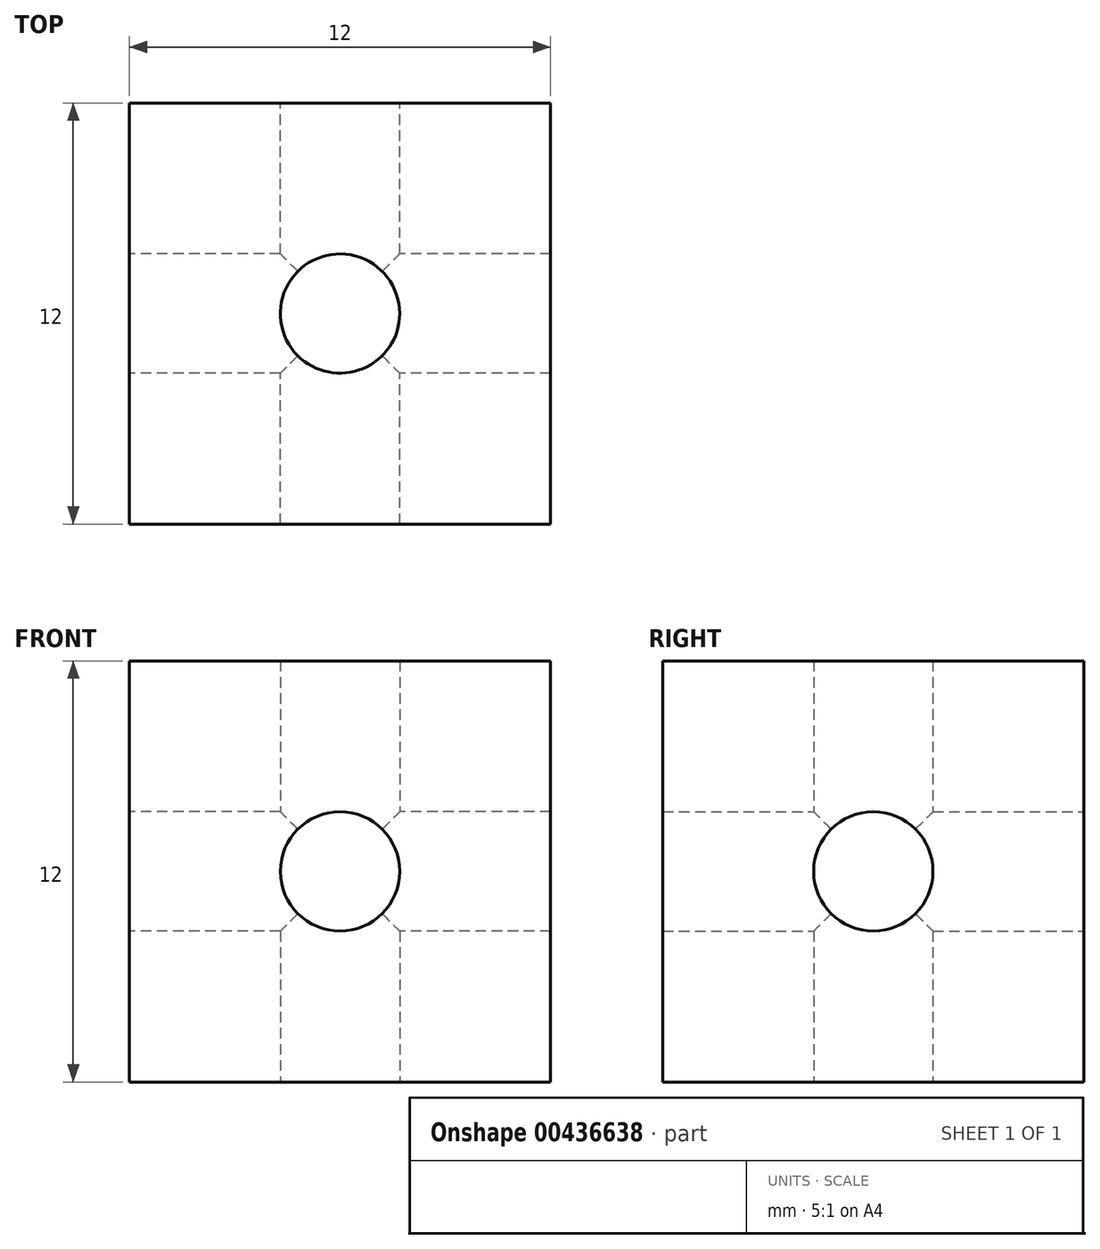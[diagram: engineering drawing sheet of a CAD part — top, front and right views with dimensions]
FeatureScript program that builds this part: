
annotation { "Feature Type Name" : "Feature", "Feature Type Description" : "" }
export const myFeature = defineFeature(function(context is Context, id is Id, definition is map)
    precondition{}
    {
        {
            var Q0;
            Q0=qCreatedBy(makeId("Top.planeOp"),FACE);
            var sketch = newSketch(context, id + "F0", { "sketchPlane" : qUnion([Q0])});
            skLineSegment(sketch, "E0.bottom", {"start": v(6, 6) * mm, "end": v(-6, 6) * mm});
            skLineSegment(sketch, "E0.top", {"start": v(6, -6) * mm, "end": v(-6, -6) * mm});
            skLineSegment(sketch, "E0.left", {"start": v(6, 6) * mm, "end": v(6, -6) * mm});
            skLineSegment(sketch, "E0.right", {"start": v(-6, 6) * mm, "end": v(-6, -6) * mm});
            skPoint(sketch, "E0.middle", {"position": v(0, 0) * mm});
            skCircle(sketch, "E1", {"center": v(0, 0) * mm, "radius": 1.7 * mm});
            skSolve(sketch);
        }
        {
            var Q0;
            Q0=makeQuery(id+"F0.imprint","IMPRINT",FACE,{"disambiguationData":[TD([[makeQuery(id+"F0.imprint","IMPRINT",EDGE,{"derivedFrom":sQuery(id+"F0.wireOp",EDGE,"E0.bottom")}),1.0]])]});
            extrude(context, id + "F1", {"entities" : qUnion([Q0]), "depth" : 12 * mm});
        }
        {
            var Q0;
            Q0=makeQuery(id+"F1.opExtrude","SWEPT_FACE",FACE,{"disambiguationData":[OSD([sQuery(id+"F0.wireOp",EDGE,"E0.right")])]});
            var sketch = newSketch(context, id + "F2", { "sketchPlane" : qUnion([Q0])});
            skLineSegment(sketch, "E2", {"start": v(0, 0) * mm, "end": v(0, 6) * mm, "construction": true});
            skPoint(sketch, "E2.endSnap0", {"position": v(0, 0) * mm});
            skCircle(sketch, "E3", {"center": v(0, 6) * mm, "radius": 1.7 * mm});
            skSolve(sketch);
        }
        {
            var Q0;
            Q0=makeQuery(id+"F2.imprint","IMPRINT",FACE,{"disambiguationData":[TD([[makeQuery(id+"F2.imprint","IMPRINT",EDGE,{"derivedFrom":sQuery(id+"F2.wireOp",EDGE,"E3")}),1.0]])]});
            extrude(context, id + "F3", {"entities" : qUnion([Q0]), "operationType" : NewBodyOperationType.REMOVE, "oppositeDirection" : true, "depth" : 12 * mm});
        }
        {
            var Q0;
            Q0=makeQuery(id+"F1.opExtrude","SWEPT_FACE",FACE,{"disambiguationData":[OSD([sQuery(id+"F0.wireOp",EDGE,"E0.bottom")])]});
            var sketch = newSketch(context, id + "F4", { "sketchPlane" : qUnion([Q0])});
            skLineSegment(sketch, "E4", {"start": v(0, 0) * mm, "end": v(0, 6) * mm, "construction": true});
            skPoint(sketch, "E4.endSnap0", {"position": v(0, 0) * mm});
            skCircle(sketch, "E5", {"center": v(0, 6) * mm, "radius": 1.7 * mm});
            skSolve(sketch);
        }
        {
            var Q0;
            Q0=makeQuery(id+"F4.imprint","IMPRINT",FACE,{"disambiguationData":[TD([[makeQuery(id+"F4.imprint","IMPRINT",EDGE,{"derivedFrom":sQuery(id+"F4.wireOp",EDGE,"E5")}),1.0]])]});
            extrude(context, id + "F5", {"entities" : qUnion([Q0]), "operationType" : NewBodyOperationType.REMOVE, "oppositeDirection" : true, "depth" : 12 * mm});
        }
    });
